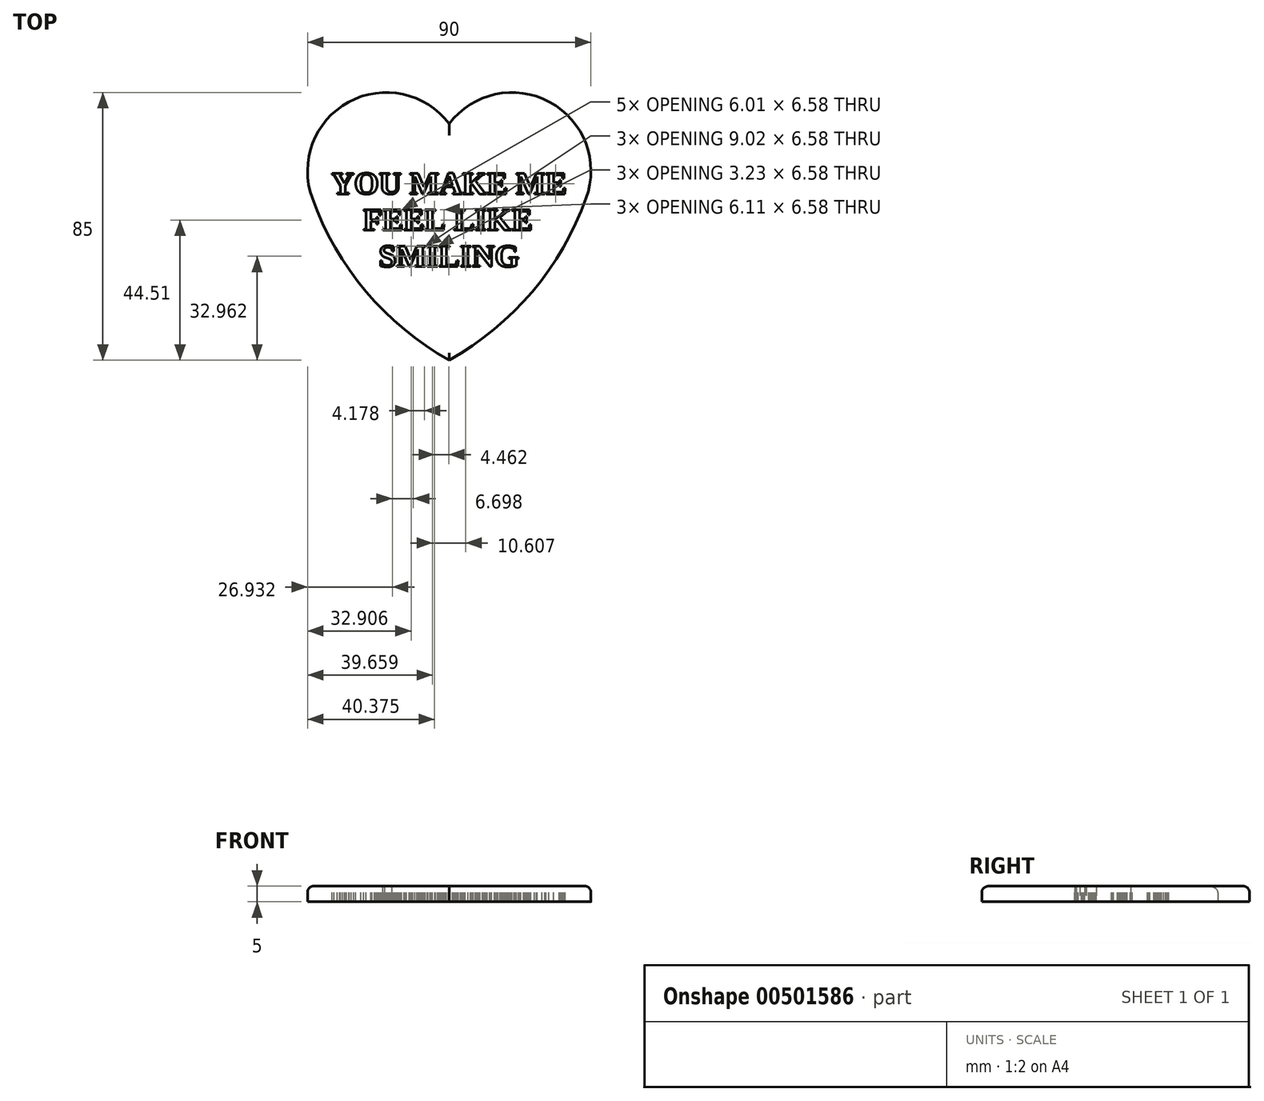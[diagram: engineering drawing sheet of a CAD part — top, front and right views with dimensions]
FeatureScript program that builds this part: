
annotation { "Feature Type Name" : "Feature", "Feature Type Description" : "" }
export const myFeature = defineFeature(function(context is Context, id is Id, definition is map)
    precondition{}
    {
        {
            var Q0;
            Q0=qCreatedBy(makeId("Top.planeOp"),FACE);
            var sketch = newSketch(context, id + "F0", { "sketchPlane" : qUnion([Q0])});
            skArc(sketch, "E0", {"start": v(-43.47, 1.39) * mm, "mid": v(-26.4, -28.25) * mm, "end": v(0, -50) * mm});
            skArc(sketch, "E1", {"start": v(0, 25) * mm, "mid": v(-31.93, 31.97) * mm, "end": v(-43.47, 1.39) * mm});
            skArc(sketch, "E2.MirrorCS", {"start": v(0, 25) * mm, "mid": v(31.93, 31.97) * mm, "end": v(43.47, 1.39) * mm});
            skArc(sketch, "E3.MirrorCS", {"start": v(43.47, 1.39) * mm, "mid": v(26.4, -28.25) * mm, "end": v(0, -50) * mm});
            skSolve(sketch);
        }
        {
            var Q0;
            Q0 = qSketchRegion(id + "F0", true);
            extrude(context, id + "F1", {"entities" : qUnion([Q0]), "depth" : 5 * mm});
        }
        {
            var Q0;
            Q0=makeQuery(id+"F1.opExtrude","CAP_FACE",FACE,{"disambiguationData":[OSD([sQuery(id+"F0.wireOp",EDGE,"E0"),sQuery(id+"F0.wireOp",EDGE,"E1"),sQuery(id+"F0.wireOp",EDGE,"E2.MirrorCS"),sQuery(id+"F0.wireOp",EDGE,"E3.MirrorCS")])],"isStart":false});
            var sketch = newSketch(context, id + "F2", { "sketchPlane" : qUnion([Q0])});
            skText(sketch, "E4", { "text": "YOU MAKE ME   \n    FEEL LIKE \n      SMILING", "fontName": "Tinos-Bold.ttf"});
            const initialGuessF2  = {"E4": [-0.03742, 0.00277, 1, 0, 0.00723]};
            skSetInitialGuess(sketch, initialGuessF2);
            skSolve(sketch);
        }
        {
            var Q0;
            Q0 = qSketchRegion(id + "F2", true);
            extrude(context, id + "F3", {"entities" : qUnion([Q0]), "operationType" : NewBodyOperationType.REMOVE, "oppositeDirection" : true, "depth" : 5 * mm});
        }
        {
            var Q0;
            Q0=makeQuery(id+"F1.opExtrude","CAP_EDGE",EDGE,{"disambiguationData":[OSD([sQuery(id+"F0.wireOp",EDGE,"E3.MirrorCS")])],"isStart":false});
            var Q1;
            Q1=makeQuery(id+"F1.opExtrude","CAP_EDGE",EDGE,{"disambiguationData":[OSD([sQuery(id+"F0.wireOp",EDGE,"E2.MirrorCS")])],"isStart":false});
            var Q2;
            Q2=makeQuery(id+"F1.opExtrude","CAP_EDGE",EDGE,{"disambiguationData":[OSD([sQuery(id+"F0.wireOp",EDGE,"E1")])],"isStart":false});
            fillet(context, id + "F4", {"entities" : qUnion([Q0, Q1, Q2]), "radius" : 2 * mm, "tangentPropagation" : true, "allowEdgeOverflow" : false});
        }
    });
